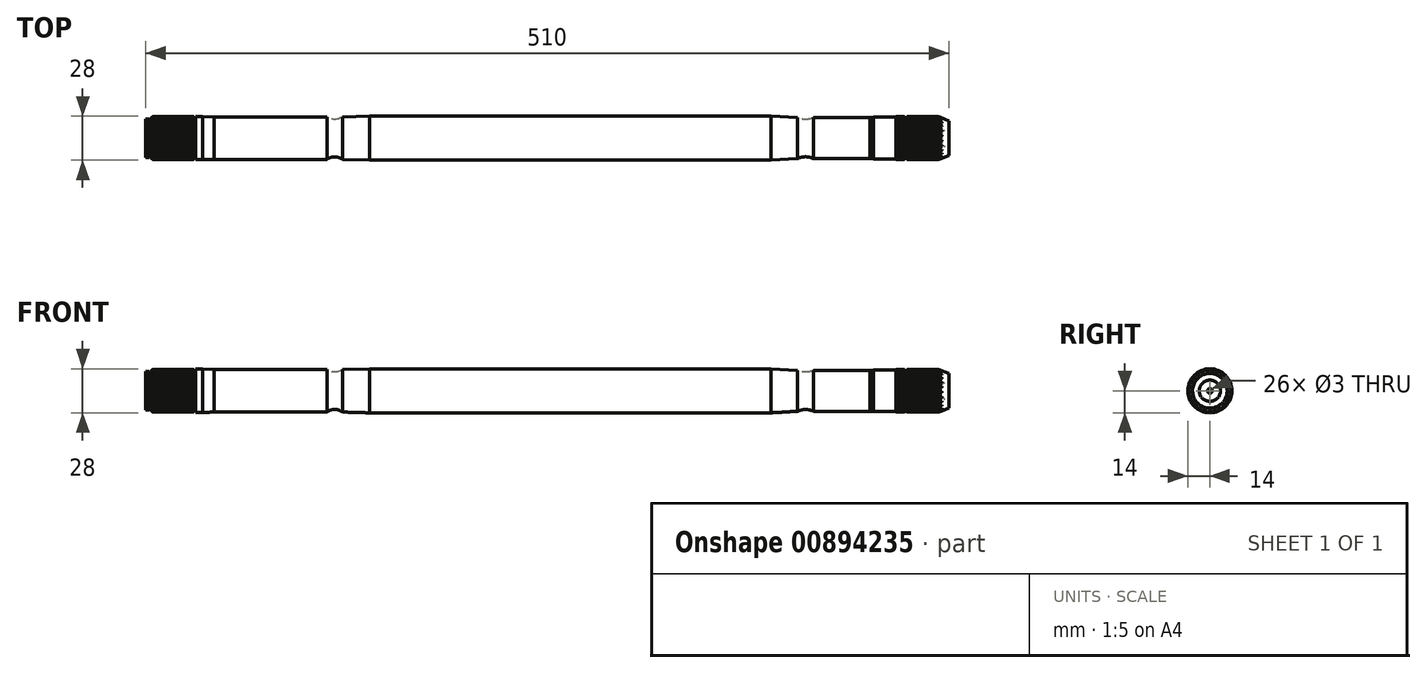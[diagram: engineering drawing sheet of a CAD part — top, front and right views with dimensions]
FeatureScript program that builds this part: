
annotation { "Feature Type Name" : "Feature", "Feature Type Description" : "" }
export const myFeature = defineFeature(function(context is Context, id is Id, definition is map)
    precondition{}
    {
        {
            var Q0;
            Q0=qCreatedBy(makeId("Front.planeOp"),FACE);
            var sketch = newSketch(context, id + "F0", { "sketchPlane" : qUnion([Q0])});
            skLineSegment(sketch, "E0", {"start": v(476.5, 13.25) * mm, "end": v(476.5, 13.75) * mm});
            skLineSegment(sketch, "E1", {"start": v(462, 13.25) * mm, "end": v(476.5, 13.25) * mm});
            skLineSegment(sketch, "E2", {"start": v(460, 13) * mm, "end": v(462, 13.25) * mm});
            skLineSegment(sketch, "E3", {"start": v(424, 13) * mm, "end": v(460, 13) * mm});
            skArc(sketch, "E4", {"start": v(414, 13) * mm, "mid": v(419, 11.85) * mm, "end": v(424, 13) * mm});
            skLineSegment(sketch, "E5", {"start": v(397, 14) * mm, "end": v(414, 13) * mm});
            skLineSegment(sketch, "E6", {"start": v(498, 0) * mm, "end": v(499, 1.5) * mm});
            skLineSegment(sketch, "E7", {"start": v(499, 1.5) * mm, "end": v(501, 1.5) * mm});
            skLineSegment(sketch, "E8", {"start": v(510, 6.75) * mm, "end": v(501, 1.5) * mm});
            skLineSegment(sketch, "E9", {"start": v(0, 6.75) * mm, "end": v(0, 12.2) * mm});
            skLineSegment(sketch, "E10", {"start": v(0, 12.2) * mm, "end": v(2, 12.2) * mm});
            skLineSegment(sketch, "E11", {"start": v(2, 12.2) * mm, "end": v(2, 11.43) * mm});
            skLineSegment(sketch, "E12", {"start": v(3.5, 11.43) * mm, "end": v(3.5, 12.75) * mm});
            skLineSegment(sketch, "E13", {"start": v(4.5, 13.75) * mm, "end": v(30, 13.75) * mm});
            skLineSegment(sketch, "E14", {"start": v(31, 12.75) * mm, "end": v(31.5, 12.75) * mm});
            skLineSegment(sketch, "E15", {"start": v(31.5, 13.75) * mm, "end": v(36, 13.75) * mm});
            skLineSegment(sketch, "E16", {"start": v(31.5, 13.75) * mm, "end": v(31.5, 12.75) * mm});
            skLineSegment(sketch, "E17", {"start": v(36, 13.75) * mm, "end": v(43.5, 13.5) * mm});
            skLineSegment(sketch, "E18", {"start": v(43.5, 13.5) * mm, "end": v(115, 13.5) * mm});
            skArc(sketch, "E19", {"start": v(115, 13.5) * mm, "mid": v(120, 11.85) * mm, "end": v(125, 13.5) * mm});
            skLineSegment(sketch, "E20", {"start": v(31, 12.75) * mm, "end": v(30, 13.75) * mm});
            skLineSegment(sketch, "E21", {"start": v(498, 0) * mm, "end": v(12, 0) * mm});
            skLineSegment(sketch, "E22", {"start": v(397, 14) * mm, "end": v(142, 14) * mm});
            skLineSegment(sketch, "E23", {"start": v(0, 6.75) * mm, "end": v(9.1, 1.5) * mm});
            skLineSegment(sketch, "E24", {"start": v(11.1, 1.5) * mm, "end": v(9.1, 1.5) * mm});
            skLineSegment(sketch, "E25", {"start": v(483.5, 13.75) * mm, "end": v(503, 13.75) * mm});
            skLineSegment(sketch, "E26", {"start": v(510, 6.75) * mm, "end": v(510, 11) * mm});
            skLineSegment(sketch, "E27", {"start": v(503, 13.75) * mm, "end": v(510, 11) * mm});
            skLineSegment(sketch, "E28", {"start": v(481.7, 13) * mm, "end": v(483.5, 13) * mm});
            skLineSegment(sketch, "E29", {"start": v(481.7, 13.75) * mm, "end": v(476.5, 13.75) * mm});
            skLineSegment(sketch, "E30", {"start": v(3.5, 11.43) * mm, "end": v(2, 11.43) * mm});
            skLineSegment(sketch, "E31", {"start": v(481.7, 13.75) * mm, "end": v(481.7, 13) * mm});
            skLineSegment(sketch, "E32", {"start": v(483.5, 13.75) * mm, "end": v(483.5, 13) * mm});
            skLineSegment(sketch, "E33", {"start": v(11.1, 1.5) * mm, "end": v(12, 0) * mm});
            skLineSegment(sketch, "E34", {"start": v(125, 13.5) * mm, "end": v(142, 14) * mm});
            skLineSegment(sketch, "E35", {"start": v(4.5, 13.75) * mm, "end": v(3.5, 12.75) * mm});
            skSolve(sketch);
        }
        {
            var Q0;
            Q0=qSketchRegion(id+"F0",true);
            var Q1;
            Q1=sQuery(id+"F0.wireOp",EDGE,"E21");
            revolve(context, id + "F1", {"surfaceOperationType" : NewSurfaceOperationType.NEW, "entities" : qUnion([Q0]), "axis" : qUnion([Q1]), "revolveType" : RevolveType.FULL});
        }
        {
            var Q0;
            Q0=qCreatedBy(makeId("Right.planeOp"),FACE);
            var sketch = newSketch(context, id + "F2", { "sketchPlane" : qUnion([Q0])});
            skArc(sketch, "E36", {"start": v(0.5, 13.56) * mm, "mid": v(0.25, 13.57) * mm, "end": v(0, 13.57) * mm});
            skArc(sketch, "E37", {"start": v(1.6, 12.57) * mm, "mid": v(1.47, 12.59) * mm, "end": v(1.34, 12.6) * mm});
            skLineSegment(sketch, "E38", {"start": v(1.34, 12.6) * mm, "end": v(0.5, 13.56) * mm});
            skArc(sketch, "E39", {"start": v(0, 13.57) * mm, "mid": v(-0.25, 13.57) * mm, "end": v(-0.5, 13.56) * mm});
            skArc(sketch, "E40", {"start": v(-1.34, 12.6) * mm, "mid": v(-1.47, 12.59) * mm, "end": v(-1.6, 12.57) * mm});
            skLineSegment(sketch, "E41", {"start": v(-1.34, 12.6) * mm, "end": v(-0.5, 13.56) * mm});
            skArc(sketch, "E42", {"start": v(-2.9, 13.26) * mm, "mid": v(-3.14, 13.2) * mm, "end": v(-3.38, 13.15) * mm});
            skArc(sketch, "E43", {"start": v(-1.6, 12.57) * mm, "mid": v(-1.72, 12.56) * mm, "end": v(-1.84, 12.54) * mm});
            skLineSegment(sketch, "E44", {"start": v(-1.84, 12.54) * mm, "end": v(-2.9, 13.26) * mm});
            skArc(sketch, "E45", {"start": v(-3.38, 13.15) * mm, "mid": v(-3.62, 13.08) * mm, "end": v(-3.86, 13.01) * mm});
            skArc(sketch, "E46", {"start": v(-4.44, 11.87) * mm, "mid": v(-4.56, 11.83) * mm, "end": v(-4.68, 11.78) * mm});
            skLineSegment(sketch, "E47", {"start": v(-4.44, 11.87) * mm, "end": v(-3.86, 13.01) * mm});
            skArc(sketch, "E48", {"start": v(-6.1, 12.12) * mm, "mid": v(-6.33, 12) * mm, "end": v(-6.55, 11.9) * mm});
            skArc(sketch, "E49", {"start": v(-4.68, 11.78) * mm, "mid": v(-4.8, 11.73) * mm, "end": v(-4.9, 11.69) * mm});
            skLineSegment(sketch, "E50", {"start": v(-4.9, 11.69) * mm, "end": v(-6.1, 12.12) * mm});
            skArc(sketch, "E51", {"start": v(-6.55, 11.9) * mm, "mid": v(-6.77, 11.77) * mm, "end": v(-6.99, 11.64) * mm});
            skArc(sketch, "E52", {"start": v(-7.26, 10.4) * mm, "mid": v(-7.36, 10.32) * mm, "end": v(-7.46, 10.25) * mm});
            skLineSegment(sketch, "E53", {"start": v(-7.26, 10.4) * mm, "end": v(-6.99, 11.64) * mm});
            skArc(sketch, "E54", {"start": v(-8.94, 10.22) * mm, "mid": v(-9.13, 10.06) * mm, "end": v(-9.3, 9.89) * mm});
            skArc(sketch, "E55", {"start": v(-7.46, 10.25) * mm, "mid": v(-7.57, 10.17) * mm, "end": v(-7.67, 10.1) * mm});
            skLineSegment(sketch, "E56", {"start": v(-7.67, 10.1) * mm, "end": v(-8.94, 10.22) * mm});
            skArc(sketch, "E57", {"start": v(-9.3, 9.89) * mm, "mid": v(-9.5, 9.71) * mm, "end": v(-9.67, 9.54) * mm});
            skArc(sketch, "E58", {"start": v(-9.62, 8.26) * mm, "mid": v(-9.7, 8.17) * mm, "end": v(-9.79, 8.07) * mm});
            skLineSegment(sketch, "E59", {"start": v(-9.62, 8.26) * mm, "end": v(-9.67, 9.54) * mm});
            skArc(sketch, "E60", {"start": v(-11.2, 7.68) * mm, "mid": v(-11.35, 7.47) * mm, "end": v(-11.48, 7.26) * mm});
            skArc(sketch, "E61", {"start": v(-9.79, 8.07) * mm, "mid": v(-9.87, 7.97) * mm, "end": v(-9.94, 7.87) * mm});
            skLineSegment(sketch, "E62", {"start": v(-9.94, 7.87) * mm, "end": v(-11.2, 7.68) * mm});
            skArc(sketch, "E63", {"start": v(-11.48, 7.26) * mm, "mid": v(-11.61, 7.05) * mm, "end": v(-11.74, 6.83) * mm});
            skArc(sketch, "E64", {"start": v(-11.38, 5.6) * mm, "mid": v(-11.44, 5.5) * mm, "end": v(-11.5, 5.38) * mm});
            skLineSegment(sketch, "E65", {"start": v(-11.38, 5.6) * mm, "end": v(-11.74, 6.83) * mm});
            skArc(sketch, "E66", {"start": v(-12.77, 4.65) * mm, "mid": v(-12.85, 4.41) * mm, "end": v(-12.93, 4.18) * mm});
            skArc(sketch, "E67", {"start": v(-11.5, 5.38) * mm, "mid": v(-11.54, 5.27) * mm, "end": v(-11.6, 5.15) * mm});
            skLineSegment(sketch, "E68", {"start": v(-11.6, 5.15) * mm, "end": v(-12.77, 4.65) * mm});
            skArc(sketch, "E69", {"start": v(-12.93, 4.18) * mm, "mid": v(-13, 3.94) * mm, "end": v(-13.08, 3.7) * mm});
            skArc(sketch, "E70", {"start": v(-12.43, 2.6) * mm, "mid": v(-12.45, 2.48) * mm, "end": v(-12.48, 2.35) * mm});
            skLineSegment(sketch, "E71", {"start": v(-12.43, 2.6) * mm, "end": v(-13.08, 3.7) * mm});
            skArc(sketch, "E72", {"start": v(-13.53, 1.33) * mm, "mid": v(-13.56, 1.08) * mm, "end": v(-13.57, 0.83) * mm});
            skArc(sketch, "E73", {"start": v(-12.48, 2.35) * mm, "mid": v(-12.5, 2.23) * mm, "end": v(-12.52, 2.1) * mm});
            skLineSegment(sketch, "E74", {"start": v(-12.52, 2.1) * mm, "end": v(-13.53, 1.33) * mm});
            skArc(sketch, "E75", {"start": v(-13.57, 0.83) * mm, "mid": v(-13.59, 0.58) * mm, "end": v(-13.6, 0.33) * mm});
            skArc(sketch, "E76", {"start": v(-12.69, -0.57) * mm, "mid": v(-12.68, -0.7) * mm, "end": v(-12.67, -0.82) * mm});
            skLineSegment(sketch, "E77", {"start": v(-12.69, -0.57) * mm, "end": v(-13.6, 0.33) * mm});
            skArc(sketch, "E78", {"start": v(-13.44, -2.08) * mm, "mid": v(-13.4, -2.33) * mm, "end": v(-13.36, -2.58) * mm});
            skArc(sketch, "E79", {"start": v(-12.67, -0.82) * mm, "mid": v(-12.67, -0.95) * mm, "end": v(-12.66, -1.08) * mm});
            skLineSegment(sketch, "E80", {"start": v(-12.66, -1.08) * mm, "end": v(-13.44, -2.08) * mm});
            skArc(sketch, "E81", {"start": v(-13.36, -2.58) * mm, "mid": v(-13.3, -2.82) * mm, "end": v(-13.26, -3.06) * mm});
            skArc(sketch, "E82", {"start": v(-12.15, -3.71) * mm, "mid": v(-12.12, -3.83) * mm, "end": v(-12.08, -3.95) * mm});
            skLineSegment(sketch, "E83", {"start": v(-12.15, -3.71) * mm, "end": v(-13.26, -3.06) * mm});
            skArc(sketch, "E84", {"start": v(-12.51, -5.36) * mm, "mid": v(-12.41, -5.6) * mm, "end": v(-12.3, -5.82) * mm});
            skArc(sketch, "E85", {"start": v(-12.08, -3.95) * mm, "mid": v(-12.04, -4.07) * mm, "end": v(-12, -4.2) * mm});
            skLineSegment(sketch, "E86", {"start": v(-12, -4.2) * mm, "end": v(-12.51, -5.36) * mm});
            skArc(sketch, "E87", {"start": v(-12.3, -5.82) * mm, "mid": v(-12.2, -6.04) * mm, "end": v(-12.08, -6.27) * mm});
            skArc(sketch, "E88", {"start": v(-10.86, -6.62) * mm, "mid": v(-10.79, -6.73) * mm, "end": v(-10.72, -6.83) * mm});
            skLineSegment(sketch, "E89", {"start": v(-10.86, -6.62) * mm, "end": v(-12.08, -6.27) * mm});
            skArc(sketch, "E90", {"start": v(-10.8, -8.3) * mm, "mid": v(-10.64, -8.5) * mm, "end": v(-10.48, -8.7) * mm});
            skArc(sketch, "E91", {"start": v(-10.72, -6.83) * mm, "mid": v(-10.65, -6.94) * mm, "end": v(-10.59, -7.04) * mm});
            skLineSegment(sketch, "E92", {"start": v(-10.59, -7.04) * mm, "end": v(-10.8, -8.3) * mm});
            skArc(sketch, "E93", {"start": v(-10.48, -8.7) * mm, "mid": v(-10.32, -8.89) * mm, "end": v(-10.15, -9.08) * mm});
            skArc(sketch, "E94", {"start": v(-8.88, -9.11) * mm, "mid": v(-8.79, -9.2) * mm, "end": v(-8.7, -9.28) * mm});
            skLineSegment(sketch, "E95", {"start": v(-8.88, -9.11) * mm, "end": v(-10.15, -9.08) * mm});
            skArc(sketch, "E96", {"start": v(-8.4, -10.73) * mm, "mid": v(-8.2, -10.88) * mm, "end": v(-8, -11.03) * mm});
            skArc(sketch, "E97", {"start": v(-8.7, -9.28) * mm, "mid": v(-8.6, -9.37) * mm, "end": v(-8.5, -9.46) * mm});
            skLineSegment(sketch, "E98", {"start": v(-8.5, -9.46) * mm, "end": v(-8.4, -10.73) * mm});
            skArc(sketch, "E99", {"start": v(-8, -11.03) * mm, "mid": v(-7.8, -11.17) * mm, "end": v(-7.58, -11.32) * mm});
            skArc(sketch, "E100", {"start": v(-6.34, -11.03) * mm, "mid": v(-6.23, -11.1) * mm, "end": v(-6.12, -11.16) * mm});
            skLineSegment(sketch, "E101", {"start": v(-6.34, -11.03) * mm, "end": v(-7.58, -11.32) * mm});
            skArc(sketch, "E102", {"start": v(-5.47, -12.48) * mm, "mid": v(-5.24, -12.58) * mm, "end": v(-5, -12.67) * mm});
            skArc(sketch, "E103", {"start": v(-6.12, -11.16) * mm, "mid": v(-6, -11.22) * mm, "end": v(-5.9, -11.28) * mm});
            skLineSegment(sketch, "E104", {"start": v(-5.9, -11.28) * mm, "end": v(-5.47, -12.48) * mm});
            skArc(sketch, "E105", {"start": v(-5, -12.67) * mm, "mid": v(-4.77, -12.76) * mm, "end": v(-4.54, -12.85) * mm});
            skArc(sketch, "E106", {"start": v(-3.4, -12.26) * mm, "mid": v(-3.28, -12.3) * mm, "end": v(-3.16, -12.33) * mm});
            skLineSegment(sketch, "E107", {"start": v(-3.4, -12.26) * mm, "end": v(-4.54, -12.85) * mm});
            skArc(sketch, "E108", {"start": v(-2.2, -13.45) * mm, "mid": v(-1.95, -13.49) * mm, "end": v(-1.7, -13.52) * mm});
            skArc(sketch, "E109", {"start": v(-3.16, -12.33) * mm, "mid": v(-3.04, -12.36) * mm, "end": v(-2.91, -12.39) * mm});
            skLineSegment(sketch, "E110", {"start": v(-2.91, -12.39) * mm, "end": v(-2.2, -13.45) * mm});
            skArc(sketch, "E111", {"start": v(-1.7, -13.52) * mm, "mid": v(-1.46, -13.55) * mm, "end": v(-1.2, -13.57) * mm});
            skArc(sketch, "E112", {"start": v(-0.25, -12.72) * mm, "mid": v(-0.13, -12.73) * mm, "end": v(0, -12.73) * mm});
            skLineSegment(sketch, "E113", {"start": v(-0.25, -12.72) * mm, "end": v(-1.2, -13.57) * mm});
            skArc(sketch, "E114", {"start": v(1.2, -13.57) * mm, "mid": v(1.46, -13.55) * mm, "end": v(1.7, -13.52) * mm});
            skArc(sketch, "E115", {"start": v(0, -12.73) * mm, "mid": v(0.13, -12.73) * mm, "end": v(0.25, -12.72) * mm});
            skLineSegment(sketch, "E116", {"start": v(0.25, -12.72) * mm, "end": v(1.2, -13.57) * mm});
            skArc(sketch, "E117", {"start": v(1.7, -13.52) * mm, "mid": v(1.95, -13.49) * mm, "end": v(2.2, -13.45) * mm});
            skArc(sketch, "E118", {"start": v(2.91, -12.39) * mm, "mid": v(3.04, -12.36) * mm, "end": v(3.16, -12.33) * mm});
            skLineSegment(sketch, "E119", {"start": v(2.91, -12.39) * mm, "end": v(2.2, -13.45) * mm});
            skArc(sketch, "E120", {"start": v(4.54, -12.85) * mm, "mid": v(4.77, -12.76) * mm, "end": v(5, -12.67) * mm});
            skArc(sketch, "E121", {"start": v(3.16, -12.33) * mm, "mid": v(3.28, -12.3) * mm, "end": v(3.4, -12.26) * mm});
            skLineSegment(sketch, "E122", {"start": v(3.4, -12.26) * mm, "end": v(4.54, -12.85) * mm});
            skArc(sketch, "E123", {"start": v(5, -12.67) * mm, "mid": v(5.24, -12.58) * mm, "end": v(5.47, -12.48) * mm});
            skArc(sketch, "E124", {"start": v(5.9, -11.28) * mm, "mid": v(6, -11.22) * mm, "end": v(6.12, -11.16) * mm});
            skLineSegment(sketch, "E125", {"start": v(5.9, -11.28) * mm, "end": v(5.47, -12.48) * mm});
            skArc(sketch, "E126", {"start": v(7.58, -11.32) * mm, "mid": v(7.8, -11.17) * mm, "end": v(8, -11.03) * mm});
            skArc(sketch, "E127", {"start": v(6.12, -11.16) * mm, "mid": v(6.23, -11.1) * mm, "end": v(6.34, -11.03) * mm});
            skLineSegment(sketch, "E128", {"start": v(6.34, -11.03) * mm, "end": v(7.58, -11.32) * mm});
            skArc(sketch, "E129", {"start": v(8, -11.03) * mm, "mid": v(8.2, -10.88) * mm, "end": v(8.4, -10.73) * mm});
            skArc(sketch, "E130", {"start": v(8.5, -9.46) * mm, "mid": v(8.6, -9.37) * mm, "end": v(8.7, -9.28) * mm});
            skLineSegment(sketch, "E131", {"start": v(8.5, -9.46) * mm, "end": v(8.4, -10.73) * mm});
            skArc(sketch, "E132", {"start": v(10.15, -9.08) * mm, "mid": v(10.32, -8.89) * mm, "end": v(10.48, -8.7) * mm});
            skArc(sketch, "E133", {"start": v(8.7, -9.28) * mm, "mid": v(8.79, -9.2) * mm, "end": v(8.88, -9.11) * mm});
            skLineSegment(sketch, "E134", {"start": v(8.88, -9.11) * mm, "end": v(10.15, -9.08) * mm});
            skArc(sketch, "E135", {"start": v(10.48, -8.7) * mm, "mid": v(10.64, -8.5) * mm, "end": v(10.8, -8.3) * mm});
            skArc(sketch, "E136", {"start": v(10.59, -7.04) * mm, "mid": v(10.65, -6.94) * mm, "end": v(10.72, -6.83) * mm});
            skLineSegment(sketch, "E137", {"start": v(10.59, -7.04) * mm, "end": v(10.8, -8.3) * mm});
            skArc(sketch, "E138", {"start": v(12.08, -6.27) * mm, "mid": v(12.2, -6.04) * mm, "end": v(12.3, -5.82) * mm});
            skArc(sketch, "E139", {"start": v(10.72, -6.83) * mm, "mid": v(10.79, -6.73) * mm, "end": v(10.86, -6.62) * mm});
            skLineSegment(sketch, "E140", {"start": v(10.86, -6.62) * mm, "end": v(12.08, -6.27) * mm});
            skArc(sketch, "E141", {"start": v(12.3, -5.82) * mm, "mid": v(12.41, -5.6) * mm, "end": v(12.51, -5.36) * mm});
            skArc(sketch, "E142", {"start": v(12, -4.2) * mm, "mid": v(12.04, -4.07) * mm, "end": v(12.08, -3.95) * mm});
            skLineSegment(sketch, "E143", {"start": v(12, -4.2) * mm, "end": v(12.51, -5.36) * mm});
            skArc(sketch, "E144", {"start": v(13.26, -3.06) * mm, "mid": v(13.3, -2.82) * mm, "end": v(13.36, -2.58) * mm});
            skArc(sketch, "E145", {"start": v(12.08, -3.95) * mm, "mid": v(12.12, -3.83) * mm, "end": v(12.15, -3.71) * mm});
            skLineSegment(sketch, "E146", {"start": v(12.15, -3.71) * mm, "end": v(13.26, -3.06) * mm});
            skArc(sketch, "E147", {"start": v(13.36, -2.58) * mm, "mid": v(13.4, -2.33) * mm, "end": v(13.44, -2.08) * mm});
            skArc(sketch, "E148", {"start": v(12.66, -1.08) * mm, "mid": v(12.67, -0.95) * mm, "end": v(12.67, -0.82) * mm});
            skLineSegment(sketch, "E149", {"start": v(12.66, -1.08) * mm, "end": v(13.44, -2.08) * mm});
            skArc(sketch, "E150", {"start": v(13.6, 0.33) * mm, "mid": v(13.59, 0.58) * mm, "end": v(13.57, 0.83) * mm});
            skArc(sketch, "E151", {"start": v(12.67, -0.82) * mm, "mid": v(12.68, -0.7) * mm, "end": v(12.69, -0.57) * mm});
            skLineSegment(sketch, "E152", {"start": v(12.69, -0.57) * mm, "end": v(13.6, 0.33) * mm});
            skArc(sketch, "E153", {"start": v(13.57, 0.83) * mm, "mid": v(13.56, 1.08) * mm, "end": v(13.53, 1.33) * mm});
            skArc(sketch, "E154", {"start": v(12.52, 2.1) * mm, "mid": v(12.5, 2.23) * mm, "end": v(12.48, 2.35) * mm});
            skLineSegment(sketch, "E155", {"start": v(12.52, 2.1) * mm, "end": v(13.53, 1.33) * mm});
            skArc(sketch, "E156", {"start": v(13.08, 3.7) * mm, "mid": v(13, 3.94) * mm, "end": v(12.93, 4.18) * mm});
            skArc(sketch, "E157", {"start": v(12.48, 2.35) * mm, "mid": v(12.45, 2.48) * mm, "end": v(12.43, 2.6) * mm});
            skLineSegment(sketch, "E158", {"start": v(12.43, 2.6) * mm, "end": v(13.08, 3.7) * mm});
            skArc(sketch, "E159", {"start": v(12.93, 4.18) * mm, "mid": v(12.85, 4.41) * mm, "end": v(12.77, 4.65) * mm});
            skArc(sketch, "E160", {"start": v(11.6, 5.15) * mm, "mid": v(11.54, 5.27) * mm, "end": v(11.5, 5.38) * mm});
            skLineSegment(sketch, "E161", {"start": v(11.6, 5.15) * mm, "end": v(12.77, 4.65) * mm});
            skArc(sketch, "E162", {"start": v(11.74, 6.83) * mm, "mid": v(11.61, 7.05) * mm, "end": v(11.48, 7.26) * mm});
            skArc(sketch, "E163", {"start": v(11.5, 5.38) * mm, "mid": v(11.44, 5.5) * mm, "end": v(11.38, 5.6) * mm});
            skLineSegment(sketch, "E164", {"start": v(11.38, 5.6) * mm, "end": v(11.74, 6.83) * mm});
            skArc(sketch, "E165", {"start": v(11.48, 7.26) * mm, "mid": v(11.35, 7.47) * mm, "end": v(11.2, 7.68) * mm});
            skArc(sketch, "E166", {"start": v(9.94, 7.87) * mm, "mid": v(9.87, 7.97) * mm, "end": v(9.79, 8.07) * mm});
            skLineSegment(sketch, "E167", {"start": v(9.94, 7.87) * mm, "end": v(11.2, 7.68) * mm});
            skArc(sketch, "E168", {"start": v(9.67, 9.54) * mm, "mid": v(9.5, 9.71) * mm, "end": v(9.3, 9.89) * mm});
            skArc(sketch, "E169", {"start": v(9.79, 8.07) * mm, "mid": v(9.7, 8.17) * mm, "end": v(9.62, 8.26) * mm});
            skLineSegment(sketch, "E170", {"start": v(9.62, 8.26) * mm, "end": v(9.67, 9.54) * mm});
            skArc(sketch, "E171", {"start": v(9.3, 9.89) * mm, "mid": v(9.13, 10.06) * mm, "end": v(8.94, 10.22) * mm});
            skArc(sketch, "E172", {"start": v(7.67, 10.1) * mm, "mid": v(7.57, 10.17) * mm, "end": v(7.46, 10.25) * mm});
            skLineSegment(sketch, "E173", {"start": v(7.67, 10.1) * mm, "end": v(8.94, 10.22) * mm});
            skArc(sketch, "E174", {"start": v(6.99, 11.64) * mm, "mid": v(6.77, 11.77) * mm, "end": v(6.55, 11.9) * mm});
            skArc(sketch, "E175", {"start": v(7.46, 10.25) * mm, "mid": v(7.36, 10.32) * mm, "end": v(7.26, 10.4) * mm});
            skLineSegment(sketch, "E176", {"start": v(7.26, 10.4) * mm, "end": v(6.99, 11.64) * mm});
            skArc(sketch, "E177", {"start": v(6.55, 11.9) * mm, "mid": v(6.33, 12) * mm, "end": v(6.1, 12.12) * mm});
            skArc(sketch, "E178", {"start": v(4.9, 11.69) * mm, "mid": v(4.8, 11.73) * mm, "end": v(4.68, 11.78) * mm});
            skLineSegment(sketch, "E179", {"start": v(4.9, 11.69) * mm, "end": v(6.1, 12.12) * mm});
            skArc(sketch, "E180", {"start": v(3.86, 13.01) * mm, "mid": v(3.62, 13.08) * mm, "end": v(3.38, 13.15) * mm});
            skArc(sketch, "E181", {"start": v(4.68, 11.78) * mm, "mid": v(4.56, 11.83) * mm, "end": v(4.44, 11.87) * mm});
            skLineSegment(sketch, "E182", {"start": v(4.44, 11.87) * mm, "end": v(3.86, 13.01) * mm});
            skArc(sketch, "E183", {"start": v(3.38, 13.15) * mm, "mid": v(3.14, 13.2) * mm, "end": v(2.9, 13.26) * mm});
            skArc(sketch, "E184", {"start": v(1.84, 12.54) * mm, "mid": v(1.72, 12.56) * mm, "end": v(1.6, 12.57) * mm});
            skLineSegment(sketch, "E185", {"start": v(1.84, 12.54) * mm, "end": v(2.9, 13.26) * mm});
            skCircle(sketch, "E186", {"center": v(0, 0) * mm, "radius": 14.4 * mm});
            skSolve(sketch);
        }
        {
            var Q0;
            Q0=qSketchRegion(id+"F2",true);
            var Q1;
            Q1=makeQuery(id+"F1.opRevolve","SWEPT_FACE",FACE,{"disambiguationData":[OSD([sQuery(id+"F0.wireOp",EDGE,"E20")])]});
            extrude(context, id + "F3", {"entities" : qUnion([Q0]), "operationType" : NewBodyOperationType.REMOVE, "endBound" : BoundingType.UP_TO_SURFACE, "depth" : 25 * mm, "endBoundEntityFace" : qUnion([Q1]), "offsetDistance" : 25 * mm});
        }
        {
            var Q0;
            Q0=makeQuery(id+"F1.opRevolve","SWEPT_FACE",FACE,{"disambiguationData":[OSD([sQuery(id+"F0.wireOp",EDGE,"E26")])]});
            var sketch = newSketch(context, id + "F4", { "sketchPlane" : qUnion([Q0])});
            skArc(sketch, "E187", {"start": v(0.5, 13.56) * mm, "mid": v(0.25, 13.57) * mm, "end": v(0, 13.57) * mm});
            skArc(sketch, "E188", {"start": v(1.6, 12.57) * mm, "mid": v(1.47, 12.59) * mm, "end": v(1.34, 12.6) * mm});
            skLineSegment(sketch, "E189", {"start": v(1.34, 12.6) * mm, "end": v(0.5, 13.56) * mm});
            skArc(sketch, "E190", {"start": v(0, 13.57) * mm, "mid": v(-0.25, 13.57) * mm, "end": v(-0.5, 13.56) * mm});
            skArc(sketch, "E191", {"start": v(-1.34, 12.6) * mm, "mid": v(-1.47, 12.59) * mm, "end": v(-1.6, 12.57) * mm});
            skLineSegment(sketch, "E192", {"start": v(-1.34, 12.6) * mm, "end": v(-0.5, 13.56) * mm});
            skArc(sketch, "E193", {"start": v(-2.9, 13.26) * mm, "mid": v(-3.14, 13.2) * mm, "end": v(-3.38, 13.15) * mm});
            skArc(sketch, "E194", {"start": v(-1.6, 12.57) * mm, "mid": v(-1.72, 12.56) * mm, "end": v(-1.84, 12.54) * mm});
            skLineSegment(sketch, "E195", {"start": v(-1.84, 12.54) * mm, "end": v(-2.9, 13.26) * mm});
            skArc(sketch, "E196", {"start": v(-3.38, 13.15) * mm, "mid": v(-3.62, 13.08) * mm, "end": v(-3.86, 13.01) * mm});
            skArc(sketch, "E197", {"start": v(-4.44, 11.87) * mm, "mid": v(-4.56, 11.83) * mm, "end": v(-4.68, 11.78) * mm});
            skLineSegment(sketch, "E198", {"start": v(-4.44, 11.87) * mm, "end": v(-3.86, 13.01) * mm});
            skArc(sketch, "E199", {"start": v(-6.1, 12.12) * mm, "mid": v(-6.33, 12) * mm, "end": v(-6.55, 11.9) * mm});
            skArc(sketch, "E200", {"start": v(-4.68, 11.78) * mm, "mid": v(-4.8, 11.73) * mm, "end": v(-4.9, 11.69) * mm});
            skLineSegment(sketch, "E201", {"start": v(-4.9, 11.69) * mm, "end": v(-6.1, 12.12) * mm});
            skArc(sketch, "E202", {"start": v(-6.55, 11.9) * mm, "mid": v(-6.77, 11.77) * mm, "end": v(-6.99, 11.64) * mm});
            skArc(sketch, "E203", {"start": v(-7.26, 10.4) * mm, "mid": v(-7.36, 10.32) * mm, "end": v(-7.46, 10.25) * mm});
            skLineSegment(sketch, "E204", {"start": v(-7.26, 10.4) * mm, "end": v(-6.99, 11.64) * mm});
            skArc(sketch, "E205", {"start": v(-8.94, 10.22) * mm, "mid": v(-9.13, 10.06) * mm, "end": v(-9.3, 9.89) * mm});
            skArc(sketch, "E206", {"start": v(-7.46, 10.25) * mm, "mid": v(-7.57, 10.17) * mm, "end": v(-7.67, 10.1) * mm});
            skLineSegment(sketch, "E207", {"start": v(-7.67, 10.1) * mm, "end": v(-8.94, 10.22) * mm});
            skArc(sketch, "E208", {"start": v(-9.3, 9.89) * mm, "mid": v(-9.5, 9.71) * mm, "end": v(-9.67, 9.54) * mm});
            skArc(sketch, "E209", {"start": v(-9.62, 8.26) * mm, "mid": v(-9.7, 8.17) * mm, "end": v(-9.79, 8.07) * mm});
            skLineSegment(sketch, "E210", {"start": v(-9.62, 8.26) * mm, "end": v(-9.67, 9.54) * mm});
            skArc(sketch, "E211", {"start": v(-11.2, 7.68) * mm, "mid": v(-11.35, 7.47) * mm, "end": v(-11.48, 7.26) * mm});
            skArc(sketch, "E212", {"start": v(-9.79, 8.07) * mm, "mid": v(-9.87, 7.97) * mm, "end": v(-9.94, 7.87) * mm});
            skLineSegment(sketch, "E213", {"start": v(-9.94, 7.87) * mm, "end": v(-11.2, 7.68) * mm});
            skArc(sketch, "E214", {"start": v(-11.48, 7.26) * mm, "mid": v(-11.61, 7.05) * mm, "end": v(-11.74, 6.83) * mm});
            skArc(sketch, "E215", {"start": v(-11.38, 5.6) * mm, "mid": v(-11.44, 5.5) * mm, "end": v(-11.5, 5.38) * mm});
            skLineSegment(sketch, "E216", {"start": v(-11.38, 5.6) * mm, "end": v(-11.74, 6.83) * mm});
            skArc(sketch, "E217", {"start": v(-12.77, 4.65) * mm, "mid": v(-12.85, 4.41) * mm, "end": v(-12.93, 4.18) * mm});
            skArc(sketch, "E218", {"start": v(-11.5, 5.38) * mm, "mid": v(-11.54, 5.27) * mm, "end": v(-11.6, 5.15) * mm});
            skLineSegment(sketch, "E219", {"start": v(-11.6, 5.15) * mm, "end": v(-12.77, 4.65) * mm});
            skArc(sketch, "E220", {"start": v(-12.93, 4.18) * mm, "mid": v(-13, 3.94) * mm, "end": v(-13.08, 3.7) * mm});
            skArc(sketch, "E221", {"start": v(-12.43, 2.6) * mm, "mid": v(-12.45, 2.48) * mm, "end": v(-12.48, 2.35) * mm});
            skLineSegment(sketch, "E222", {"start": v(-12.43, 2.6) * mm, "end": v(-13.08, 3.7) * mm});
            skArc(sketch, "E223", {"start": v(-13.53, 1.33) * mm, "mid": v(-13.56, 1.08) * mm, "end": v(-13.57, 0.83) * mm});
            skArc(sketch, "E224", {"start": v(-12.48, 2.35) * mm, "mid": v(-12.5, 2.23) * mm, "end": v(-12.52, 2.1) * mm});
            skLineSegment(sketch, "E225", {"start": v(-12.52, 2.1) * mm, "end": v(-13.53, 1.33) * mm});
            skArc(sketch, "E226", {"start": v(-13.57, 0.83) * mm, "mid": v(-13.59, 0.58) * mm, "end": v(-13.6, 0.33) * mm});
            skArc(sketch, "E227", {"start": v(-12.69, -0.57) * mm, "mid": v(-12.68, -0.7) * mm, "end": v(-12.67, -0.82) * mm});
            skLineSegment(sketch, "E228", {"start": v(-12.69, -0.57) * mm, "end": v(-13.6, 0.33) * mm});
            skArc(sketch, "E229", {"start": v(-13.44, -2.08) * mm, "mid": v(-13.4, -2.33) * mm, "end": v(-13.36, -2.58) * mm});
            skArc(sketch, "E230", {"start": v(-12.67, -0.82) * mm, "mid": v(-12.67, -0.95) * mm, "end": v(-12.66, -1.08) * mm});
            skLineSegment(sketch, "E231", {"start": v(-12.66, -1.08) * mm, "end": v(-13.44, -2.08) * mm});
            skArc(sketch, "E232", {"start": v(-13.36, -2.58) * mm, "mid": v(-13.3, -2.82) * mm, "end": v(-13.26, -3.06) * mm});
            skArc(sketch, "E233", {"start": v(-12.15, -3.71) * mm, "mid": v(-12.12, -3.83) * mm, "end": v(-12.08, -3.95) * mm});
            skLineSegment(sketch, "E234", {"start": v(-12.15, -3.71) * mm, "end": v(-13.26, -3.06) * mm});
            skArc(sketch, "E235", {"start": v(-12.51, -5.36) * mm, "mid": v(-12.41, -5.6) * mm, "end": v(-12.3, -5.82) * mm});
            skArc(sketch, "E236", {"start": v(-12.08, -3.95) * mm, "mid": v(-12.04, -4.07) * mm, "end": v(-12, -4.2) * mm});
            skLineSegment(sketch, "E237", {"start": v(-12, -4.2) * mm, "end": v(-12.51, -5.36) * mm});
            skArc(sketch, "E238", {"start": v(-12.3, -5.82) * mm, "mid": v(-12.2, -6.04) * mm, "end": v(-12.08, -6.27) * mm});
            skArc(sketch, "E239", {"start": v(-10.86, -6.62) * mm, "mid": v(-10.79, -6.73) * mm, "end": v(-10.72, -6.83) * mm});
            skLineSegment(sketch, "E240", {"start": v(-10.86, -6.62) * mm, "end": v(-12.08, -6.27) * mm});
            skArc(sketch, "E241", {"start": v(-10.8, -8.3) * mm, "mid": v(-10.64, -8.5) * mm, "end": v(-10.48, -8.7) * mm});
            skArc(sketch, "E242", {"start": v(-10.72, -6.83) * mm, "mid": v(-10.65, -6.94) * mm, "end": v(-10.59, -7.04) * mm});
            skLineSegment(sketch, "E243", {"start": v(-10.59, -7.04) * mm, "end": v(-10.8, -8.3) * mm});
            skArc(sketch, "E244", {"start": v(-10.48, -8.7) * mm, "mid": v(-10.32, -8.89) * mm, "end": v(-10.15, -9.08) * mm});
            skArc(sketch, "E245", {"start": v(-8.88, -9.11) * mm, "mid": v(-8.79, -9.2) * mm, "end": v(-8.7, -9.28) * mm});
            skLineSegment(sketch, "E246", {"start": v(-8.88, -9.11) * mm, "end": v(-10.15, -9.08) * mm});
            skArc(sketch, "E247", {"start": v(-8.4, -10.73) * mm, "mid": v(-8.2, -10.88) * mm, "end": v(-8, -11.03) * mm});
            skArc(sketch, "E248", {"start": v(-8.7, -9.28) * mm, "mid": v(-8.6, -9.37) * mm, "end": v(-8.5, -9.46) * mm});
            skLineSegment(sketch, "E249", {"start": v(-8.5, -9.46) * mm, "end": v(-8.4, -10.73) * mm});
            skArc(sketch, "E250", {"start": v(-8, -11.03) * mm, "mid": v(-7.8, -11.17) * mm, "end": v(-7.58, -11.32) * mm});
            skArc(sketch, "E251", {"start": v(-6.34, -11.03) * mm, "mid": v(-6.23, -11.1) * mm, "end": v(-6.12, -11.16) * mm});
            skLineSegment(sketch, "E252", {"start": v(-6.34, -11.03) * mm, "end": v(-7.58, -11.32) * mm});
            skArc(sketch, "E253", {"start": v(-5.47, -12.48) * mm, "mid": v(-5.24, -12.58) * mm, "end": v(-5, -12.67) * mm});
            skArc(sketch, "E254", {"start": v(-6.12, -11.16) * mm, "mid": v(-6, -11.22) * mm, "end": v(-5.9, -11.28) * mm});
            skLineSegment(sketch, "E255", {"start": v(-5.9, -11.28) * mm, "end": v(-5.47, -12.48) * mm});
            skArc(sketch, "E256", {"start": v(-5, -12.67) * mm, "mid": v(-4.77, -12.76) * mm, "end": v(-4.54, -12.85) * mm});
            skArc(sketch, "E257", {"start": v(-3.4, -12.26) * mm, "mid": v(-3.28, -12.3) * mm, "end": v(-3.16, -12.33) * mm});
            skLineSegment(sketch, "E258", {"start": v(-3.4, -12.26) * mm, "end": v(-4.54, -12.85) * mm});
            skArc(sketch, "E259", {"start": v(-2.2, -13.45) * mm, "mid": v(-1.95, -13.49) * mm, "end": v(-1.7, -13.52) * mm});
            skArc(sketch, "E260", {"start": v(-3.16, -12.33) * mm, "mid": v(-3.04, -12.36) * mm, "end": v(-2.91, -12.39) * mm});
            skLineSegment(sketch, "E261", {"start": v(-2.91, -12.39) * mm, "end": v(-2.2, -13.45) * mm});
            skArc(sketch, "E262", {"start": v(-1.7, -13.52) * mm, "mid": v(-1.46, -13.55) * mm, "end": v(-1.2, -13.57) * mm});
            skArc(sketch, "E263", {"start": v(-0.25, -12.72) * mm, "mid": v(-0.13, -12.73) * mm, "end": v(0, -12.73) * mm});
            skLineSegment(sketch, "E264", {"start": v(-0.25, -12.72) * mm, "end": v(-1.2, -13.57) * mm});
            skArc(sketch, "E265", {"start": v(1.2, -13.57) * mm, "mid": v(1.46, -13.55) * mm, "end": v(1.7, -13.52) * mm});
            skArc(sketch, "E266", {"start": v(0, -12.73) * mm, "mid": v(0.13, -12.73) * mm, "end": v(0.25, -12.72) * mm});
            skLineSegment(sketch, "E267", {"start": v(0.25, -12.72) * mm, "end": v(1.2, -13.57) * mm});
            skArc(sketch, "E268", {"start": v(1.7, -13.52) * mm, "mid": v(1.95, -13.49) * mm, "end": v(2.2, -13.45) * mm});
            skArc(sketch, "E269", {"start": v(2.91, -12.39) * mm, "mid": v(3.04, -12.36) * mm, "end": v(3.16, -12.33) * mm});
            skLineSegment(sketch, "E270", {"start": v(2.91, -12.39) * mm, "end": v(2.2, -13.45) * mm});
            skArc(sketch, "E271", {"start": v(4.54, -12.85) * mm, "mid": v(4.77, -12.76) * mm, "end": v(5, -12.67) * mm});
            skArc(sketch, "E272", {"start": v(3.16, -12.33) * mm, "mid": v(3.28, -12.3) * mm, "end": v(3.4, -12.26) * mm});
            skLineSegment(sketch, "E273", {"start": v(3.4, -12.26) * mm, "end": v(4.54, -12.85) * mm});
            skArc(sketch, "E274", {"start": v(5, -12.67) * mm, "mid": v(5.24, -12.58) * mm, "end": v(5.47, -12.48) * mm});
            skArc(sketch, "E275", {"start": v(5.9, -11.28) * mm, "mid": v(6, -11.22) * mm, "end": v(6.12, -11.16) * mm});
            skLineSegment(sketch, "E276", {"start": v(5.9, -11.28) * mm, "end": v(5.47, -12.48) * mm});
            skArc(sketch, "E277", {"start": v(7.58, -11.32) * mm, "mid": v(7.8, -11.17) * mm, "end": v(8, -11.03) * mm});
            skArc(sketch, "E278", {"start": v(6.12, -11.16) * mm, "mid": v(6.23, -11.1) * mm, "end": v(6.34, -11.03) * mm});
            skLineSegment(sketch, "E279", {"start": v(6.34, -11.03) * mm, "end": v(7.58, -11.32) * mm});
            skArc(sketch, "E280", {"start": v(8, -11.03) * mm, "mid": v(8.2, -10.88) * mm, "end": v(8.4, -10.73) * mm});
            skArc(sketch, "E281", {"start": v(8.5, -9.46) * mm, "mid": v(8.6, -9.37) * mm, "end": v(8.7, -9.28) * mm});
            skLineSegment(sketch, "E282", {"start": v(8.5, -9.46) * mm, "end": v(8.4, -10.73) * mm});
            skArc(sketch, "E283", {"start": v(10.15, -9.08) * mm, "mid": v(10.32, -8.89) * mm, "end": v(10.48, -8.7) * mm});
            skArc(sketch, "E284", {"start": v(8.7, -9.28) * mm, "mid": v(8.79, -9.2) * mm, "end": v(8.88, -9.11) * mm});
            skLineSegment(sketch, "E285", {"start": v(8.88, -9.11) * mm, "end": v(10.15, -9.08) * mm});
            skArc(sketch, "E286", {"start": v(10.48, -8.7) * mm, "mid": v(10.64, -8.5) * mm, "end": v(10.8, -8.3) * mm});
            skArc(sketch, "E287", {"start": v(10.59, -7.04) * mm, "mid": v(10.65, -6.94) * mm, "end": v(10.72, -6.83) * mm});
            skLineSegment(sketch, "E288", {"start": v(10.59, -7.04) * mm, "end": v(10.8, -8.3) * mm});
            skArc(sketch, "E289", {"start": v(12.08, -6.27) * mm, "mid": v(12.2, -6.04) * mm, "end": v(12.3, -5.82) * mm});
            skArc(sketch, "E290", {"start": v(10.72, -6.83) * mm, "mid": v(10.79, -6.73) * mm, "end": v(10.86, -6.62) * mm});
            skLineSegment(sketch, "E291", {"start": v(10.86, -6.62) * mm, "end": v(12.08, -6.27) * mm});
            skArc(sketch, "E292", {"start": v(12.3, -5.82) * mm, "mid": v(12.41, -5.6) * mm, "end": v(12.51, -5.36) * mm});
            skArc(sketch, "E293", {"start": v(12, -4.2) * mm, "mid": v(12.04, -4.07) * mm, "end": v(12.08, -3.95) * mm});
            skLineSegment(sketch, "E294", {"start": v(12, -4.2) * mm, "end": v(12.51, -5.36) * mm});
            skArc(sketch, "E295", {"start": v(13.26, -3.06) * mm, "mid": v(13.3, -2.82) * mm, "end": v(13.36, -2.58) * mm});
            skArc(sketch, "E296", {"start": v(12.08, -3.95) * mm, "mid": v(12.12, -3.83) * mm, "end": v(12.15, -3.71) * mm});
            skLineSegment(sketch, "E297", {"start": v(12.15, -3.71) * mm, "end": v(13.26, -3.06) * mm});
            skArc(sketch, "E298", {"start": v(13.36, -2.58) * mm, "mid": v(13.4, -2.33) * mm, "end": v(13.44, -2.08) * mm});
            skArc(sketch, "E299", {"start": v(12.66, -1.08) * mm, "mid": v(12.67, -0.95) * mm, "end": v(12.67, -0.82) * mm});
            skLineSegment(sketch, "E300", {"start": v(12.66, -1.08) * mm, "end": v(13.44, -2.08) * mm});
            skArc(sketch, "E301", {"start": v(13.6, 0.33) * mm, "mid": v(13.59, 0.58) * mm, "end": v(13.57, 0.83) * mm});
            skArc(sketch, "E302", {"start": v(12.67, -0.82) * mm, "mid": v(12.68, -0.7) * mm, "end": v(12.69, -0.57) * mm});
            skLineSegment(sketch, "E303", {"start": v(12.69, -0.57) * mm, "end": v(13.6, 0.33) * mm});
            skArc(sketch, "E304", {"start": v(13.57, 0.83) * mm, "mid": v(13.56, 1.08) * mm, "end": v(13.53, 1.33) * mm});
            skArc(sketch, "E305", {"start": v(12.52, 2.1) * mm, "mid": v(12.5, 2.23) * mm, "end": v(12.48, 2.35) * mm});
            skLineSegment(sketch, "E306", {"start": v(12.52, 2.1) * mm, "end": v(13.53, 1.33) * mm});
            skArc(sketch, "E307", {"start": v(13.08, 3.7) * mm, "mid": v(13, 3.94) * mm, "end": v(12.93, 4.18) * mm});
            skArc(sketch, "E308", {"start": v(12.48, 2.35) * mm, "mid": v(12.45, 2.48) * mm, "end": v(12.43, 2.6) * mm});
            skLineSegment(sketch, "E309", {"start": v(12.43, 2.6) * mm, "end": v(13.08, 3.7) * mm});
            skArc(sketch, "E310", {"start": v(12.93, 4.18) * mm, "mid": v(12.85, 4.41) * mm, "end": v(12.77, 4.65) * mm});
            skArc(sketch, "E311", {"start": v(11.6, 5.15) * mm, "mid": v(11.54, 5.27) * mm, "end": v(11.5, 5.38) * mm});
            skLineSegment(sketch, "E312", {"start": v(11.6, 5.15) * mm, "end": v(12.77, 4.65) * mm});
            skArc(sketch, "E313", {"start": v(11.74, 6.83) * mm, "mid": v(11.61, 7.05) * mm, "end": v(11.48, 7.26) * mm});
            skArc(sketch, "E314", {"start": v(11.5, 5.38) * mm, "mid": v(11.44, 5.5) * mm, "end": v(11.38, 5.6) * mm});
            skLineSegment(sketch, "E315", {"start": v(11.38, 5.6) * mm, "end": v(11.74, 6.83) * mm});
            skArc(sketch, "E316", {"start": v(11.48, 7.26) * mm, "mid": v(11.35, 7.47) * mm, "end": v(11.2, 7.68) * mm});
            skArc(sketch, "E317", {"start": v(9.94, 7.87) * mm, "mid": v(9.87, 7.97) * mm, "end": v(9.79, 8.07) * mm});
            skLineSegment(sketch, "E318", {"start": v(9.94, 7.87) * mm, "end": v(11.2, 7.68) * mm});
            skArc(sketch, "E319", {"start": v(9.67, 9.54) * mm, "mid": v(9.5, 9.71) * mm, "end": v(9.3, 9.89) * mm});
            skArc(sketch, "E320", {"start": v(9.79, 8.07) * mm, "mid": v(9.7, 8.17) * mm, "end": v(9.62, 8.26) * mm});
            skLineSegment(sketch, "E321", {"start": v(9.62, 8.26) * mm, "end": v(9.67, 9.54) * mm});
            skArc(sketch, "E322", {"start": v(9.3, 9.89) * mm, "mid": v(9.13, 10.06) * mm, "end": v(8.94, 10.22) * mm});
            skArc(sketch, "E323", {"start": v(7.67, 10.1) * mm, "mid": v(7.57, 10.17) * mm, "end": v(7.46, 10.25) * mm});
            skLineSegment(sketch, "E324", {"start": v(7.67, 10.1) * mm, "end": v(8.94, 10.22) * mm});
            skArc(sketch, "E325", {"start": v(6.99, 11.64) * mm, "mid": v(6.77, 11.77) * mm, "end": v(6.55, 11.9) * mm});
            skArc(sketch, "E326", {"start": v(7.46, 10.25) * mm, "mid": v(7.36, 10.32) * mm, "end": v(7.26, 10.4) * mm});
            skLineSegment(sketch, "E327", {"start": v(7.26, 10.4) * mm, "end": v(6.99, 11.64) * mm});
            skArc(sketch, "E328", {"start": v(6.55, 11.9) * mm, "mid": v(6.33, 12) * mm, "end": v(6.1, 12.12) * mm});
            skArc(sketch, "E329", {"start": v(4.9, 11.69) * mm, "mid": v(4.8, 11.73) * mm, "end": v(4.68, 11.78) * mm});
            skLineSegment(sketch, "E330", {"start": v(4.9, 11.69) * mm, "end": v(6.1, 12.12) * mm});
            skArc(sketch, "E331", {"start": v(3.86, 13.01) * mm, "mid": v(3.62, 13.08) * mm, "end": v(3.38, 13.15) * mm});
            skArc(sketch, "E332", {"start": v(4.68, 11.78) * mm, "mid": v(4.56, 11.83) * mm, "end": v(4.44, 11.87) * mm});
            skLineSegment(sketch, "E333", {"start": v(4.44, 11.87) * mm, "end": v(3.86, 13.01) * mm});
            skArc(sketch, "E334", {"start": v(3.38, 13.15) * mm, "mid": v(3.14, 13.2) * mm, "end": v(2.9, 13.26) * mm});
            skArc(sketch, "E335", {"start": v(1.84, 12.54) * mm, "mid": v(1.72, 12.56) * mm, "end": v(1.6, 12.57) * mm});
            skLineSegment(sketch, "E336", {"start": v(1.84, 12.54) * mm, "end": v(2.9, 13.26) * mm});
            skCircle(sketch, "E337", {"center": v(0, -0.03) * mm, "radius": 14.43 * mm});
            skSolve(sketch);
        }
        {
            var Q0;
            Q0=qSketchRegion(id+"F4",true);
            var Q1;
            Q1=makeQuery(id+"F1.opRevolve","SWEPT_FACE",FACE,{"disambiguationData":[OSD([sQuery(id+"F0.wireOp",EDGE,"E0")])]});
            extrude(context, id + "F5", {"entities" : qUnion([Q0]), "operationType" : NewBodyOperationType.REMOVE, "endBound" : BoundingType.UP_TO_SURFACE, "oppositeDirection" : true, "depth" : 25 * mm, "endBoundEntityFace" : qUnion([Q1]), "offsetDistance" : 25 * mm});
        }
    });
